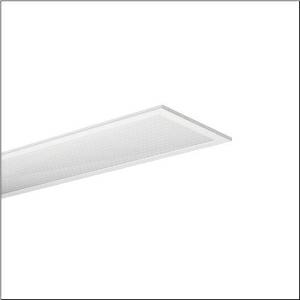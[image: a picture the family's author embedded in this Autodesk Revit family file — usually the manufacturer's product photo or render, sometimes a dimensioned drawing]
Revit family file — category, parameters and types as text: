
# Revit family: apollon_r__21_linear_51mq18wd2412_af63
name_source: partatom
category: Lighting Fixtures
units: mm (PartAtom-declared; Revit-internal decimal feet)

## family parameters
Cut with Voids When Loaded = No
Host = Face
Light Source = No
Part Type = Normal
Room Calculation Point = No
Round Connector Dimension = Use Diameter
Shared = No

## types (1)
- Apollon® 21 linear (1 x LED, 4000 lm, 33 W, 4000K)
    Apparent Load = 33 VA
    CIE Flux Codes = 60 89 97 100 100
    Color Rendering = 80
    Color Temperature = 4000K
    Default Elevation = 1800 mm
    Description = Apollon® 21 linear, office luminaire, primary optical cover: micro prismatic cover, CAT 2 (L<= 3000cd/m²), light emission: direct distribution, primary light characteristic: symmetric, installation type: lay-in mounting, LED, rated luminous flux: 4.000lm, luminous efficacy: 121lm/W, light colour: 840, colour temperature: 4000K, control gear: DALI, with terminal, 5-pole, mains connection: 220..240V, AC, 50/60Hz, rated input power: 33W, housing, of aluminium, coated, pure white, module: M600, length: 1.195mm, width: 295mm, height: 39mm, housing upper side, of sheet steel, galvanised, protection rating (complete): IP20, protection rating (lamp compartment, on room side): IP50, insulation class (complete): insulation class II (safety insulation), certification: CE, ENEC, packaging unit: 1 piece
    Height = 0 mm  [stored 0 ft]
    Lamp = 1 x LED
    Lamp Light Flux = 4000 lm
    Lamp Power = 33 W
    Lamp count = 1
    Length = 1195 mm
    Luminous efficacy = 121 lm/W
    Manufacturer = Siteco
    ModVariant = No
    Model = 51MQ18WD2412
    Mounting Place = Ceiling
    Mounting Type = Recessed
    Number of Poles = 1
    OnlyDefault = Yes
    Power Factor = 1
    Product Name = Apollon® 21 linear
    Product group = office luminaire | ceiling recessed
    ProductGroupID = 401
    Protection Class = Protection class II
    Protection Degree = IP 20
    RLX_Detail_Level = 1
    RLX_Emergency_Light_Flux = 0 lm
    RLX_Emergency_Type = 0
    RLX_Emergency_Type_DB = No
    RlxData = <blob elided: 15069 chars, md5=162b8ee2>
    Socket = socket
    Standby Power = 0 W
    System Light Flux = 4000 lm
    System Power = 33 W
    Type Comments = Product without accessories
    Type Image = l_1291045.jpg
    URL = http://relux.com
    VarID = ---
    Voltage = 0 V
    Weight = 0.00 kg
    Width = 295 mm

note: [stored X ft] marks values corroborated as IEEE doubles in the binary element streams (Revit-internal decimal feet)

## geometry (parser evidence)
native form markers: Blend x4, Sweep x10
no freeform markers — native parametric forms only
